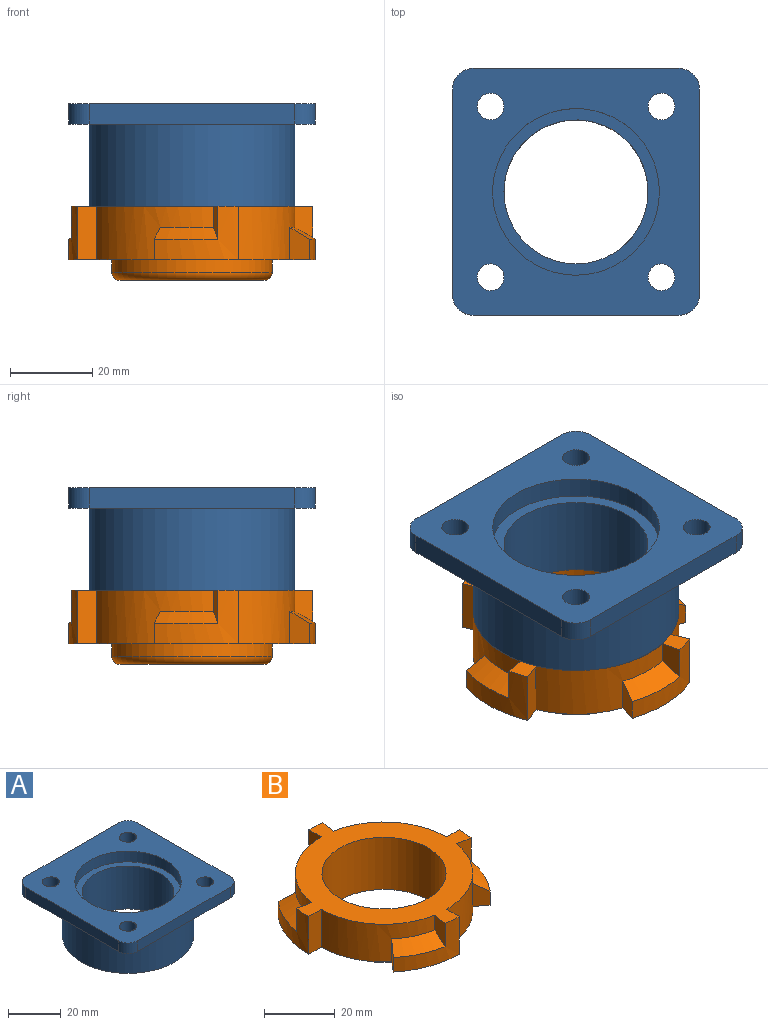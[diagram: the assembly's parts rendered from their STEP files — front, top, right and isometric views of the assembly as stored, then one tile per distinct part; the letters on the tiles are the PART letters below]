
ASSEMBLY  parts=2 mates=1
PART A: 19 faces, bbox 60x60x25 mm
  f0: plane 50x5mm, normal (0,1,0), area 250mm2, adj f9,f10,f11,f14
  f1: plane 50x5mm, normal (-1,0,0), area 250mm2, adj f9,f10,f11,f12
  f2: plane 50x5mm, normal (0,-1,0), area 250mm2, adj f9,f10,f12,f13
  f3: cylinder r=3.25mm len=6.5mm, axis (0,0,-1), area 102.1mm2, adj f9,f10
  f4: cylinder r=3.25mm len=6.5mm, axis (0,0,-1), area 102.1mm2, adj f9,f10
  f5: cylinder r=3.25mm len=6.5mm, axis (0,0,-1), area 102.1mm2, adj f9,f10
  f6: cylinder r=20.25mm len=40.5mm, axis (0,0,-1), area 636.2mm2, adj f9,f15
  f7: cylinder r=3.25mm len=6.5mm, axis (0,0,-1), area 102.1mm2, adj f9,f10
  f8: plane 50x5mm, normal (1,0,0), area 250mm2, adj f9,f10,f13,f14
  f9: plane 60x60mm, normal (0,0,1), area 2157.6mm2, adj f0,f1,f2,f3,f4,f5,f6,f7
  f10: plane 60x60mm, normal (0,0,-1), area 1482.3mm2, adj f0,f1,f2,f3,f4,f5,f7,f8
  f11: cylinder r=5mm len=5mm, axis (0,0,1), area 39.3mm2, adj f0,f1,f9,f10
  f12: cylinder r=5mm len=5mm, axis (0,0,-1), area 39.3mm2, adj f1,f2,f9,f10
  f13: cylinder r=5mm len=5mm, axis (0,0,1), area 39.3mm2, adj f2,f8,f9,f10
  f14: cylinder r=5mm len=5mm, axis (0,0,-1), area 39.3mm2, adj f0,f8,f9,f10
  f15: plane 40.5x40.5mm, normal (0,0,1), area 326.1mm2, adj f6,f16
  f16: cylinder r=17.5mm len=35mm, axis (0,0,1), area 2199.1mm2, adj f15,f18
  f17: cylinder r=25mm len=50mm, axis (0,0,1), area 3141.6mm2, adj f10,f18
  f18: plane 50x50mm, normal (0,0,-1), area 1001.4mm2, adj f16,f17
PART B: 29 faces, bbox 60x60x18 mm
  f0: cylinder r=30mm len=19.28mm, axis (0,0,-1), area 146.6mm2, adj f6,f11,f15,f20,f21,f27
  f1: cylinder r=30mm len=19.28mm, axis (0,0,-1), area 146.6mm2, adj f4,f11,f15,f22,f23,f26
  f2: cylinder r=30mm len=19.28mm, axis (0,0,-1), area 146.6mm2, adj f11,f13,f15,f16,f17,f24
  f3: cylinder r=25mm len=24.62mm, axis (0,0,-1), area 350.5mm2, adj f11,f13,f15,f17,f22,f24
  f4: cone r=30mm half-angle=60deg, axis (0,0,-1), area 83.1mm2, adj f1,f5,f23,f26
  f5: cylinder r=25mm len=24.62mm, axis (0,0,-1), area 350.5mm2, adj f4,f11,f15,f20,f23,f26
  f6: cone r=30mm half-angle=60deg, axis (0,0,-1), area 83.1mm2, adj f0,f8,f21,f27
  f7: cone r=30mm half-angle=60deg, axis (0,0,-1), area 83.1mm2, adj f12,f14,f19,f25
  f8: cylinder r=25mm len=24.62mm, axis (0,0,-1), area 350.5mm2, adj f6,f11,f15,f18,f21,f27
  f9: cylinder r=17.5mm len=35mm, axis (0,0,-1), area 1979.2mm2, adj f15,f28
  f10: cylinder r=19.5mm len=39mm, axis (0,0,-1), area 367.6mm2, adj f11,f28
  f11: plane 60x60mm, normal (0,0,-1), area 1152.9mm2, adj f0,f1,f2,f3,f5,f8,f10,f12
  f12: cylinder r=30mm len=19.28mm, axis (0,0,-1), area 146.6mm2, adj f7,f11,f15,f18,f19,f25
  f13: cone r=30mm half-angle=60deg, axis (0,0,-1), area 83.1mm2, adj f2,f3,f17,f24
  f14: cylinder r=25mm len=24.62mm, axis (0,0,-1), area 350.5mm2, adj f7,f11,f15,f16,f19,f25
  f15: plane 60x60mm, normal (0,0,1), area 1097.4mm2, adj f0,f1,f2,f3,f5,f8,f9,f12
  f16: plane 13x5mm, normal (1,0,0), area 65mm2, adj f2,f11,f14,f15
  f17: plane 8x4.92mm, normal (-0.98,0.17,0), area 32.8mm2, adj f2,f3,f13,f15
  f18: plane 13x5mm, normal (0,1,0), area 65mm2, adj f8,f11,f12,f15
  f19: plane 8x4.92mm, normal (-0.17,-0.98,0), area 32.8mm2, adj f7,f12,f14,f15
  f20: plane 13x5mm, normal (-1,0,0), area 65mm2, adj f0,f5,f11,f15
  f21: plane 8x4.92mm, normal (0.98,-0.17,0), area 32.8mm2, adj f0,f6,f8,f15
  f22: plane 13x5mm, normal (0,-1,0), area 65mm2, adj f1,f3,f11,f15
  f23: plane 8x4.92mm, normal (0.17,0.98,0), area 32.8mm2, adj f1,f4,f5,f15
  f24: plane 7.89x3.83mm, normal (-0.77,0.64,0), area 32.2mm2, adj f2,f3,f11,f13
  f25: plane 7.89x3.83mm, normal (-0.64,-0.77,0), area 32.2mm2, adj f7,f11,f12,f14
  f26: plane 7.89x3.83mm, normal (0.64,0.77,0), area 32.2mm2, adj f1,f4,f5,f11
  f27: plane 7.89x3.83mm, normal (0.77,-0.64,0), area 32.2mm2, adj f0,f6,f8,f11
  f28: torus R=17.5mm, axis (0,0,-1), area 370.6mm2, adj f9,f10
PLACE A t=(-7.81,11.99,-19.52)mm fixed
PLACE B rot(axis=(0,0,1),22.1deg) t=(-7.81,11.99,-57.52)mm
MATE revolute A.f17 <-> B.f0  axis (0,0,-1) through (-7.81,11.99,-39.52)mm
